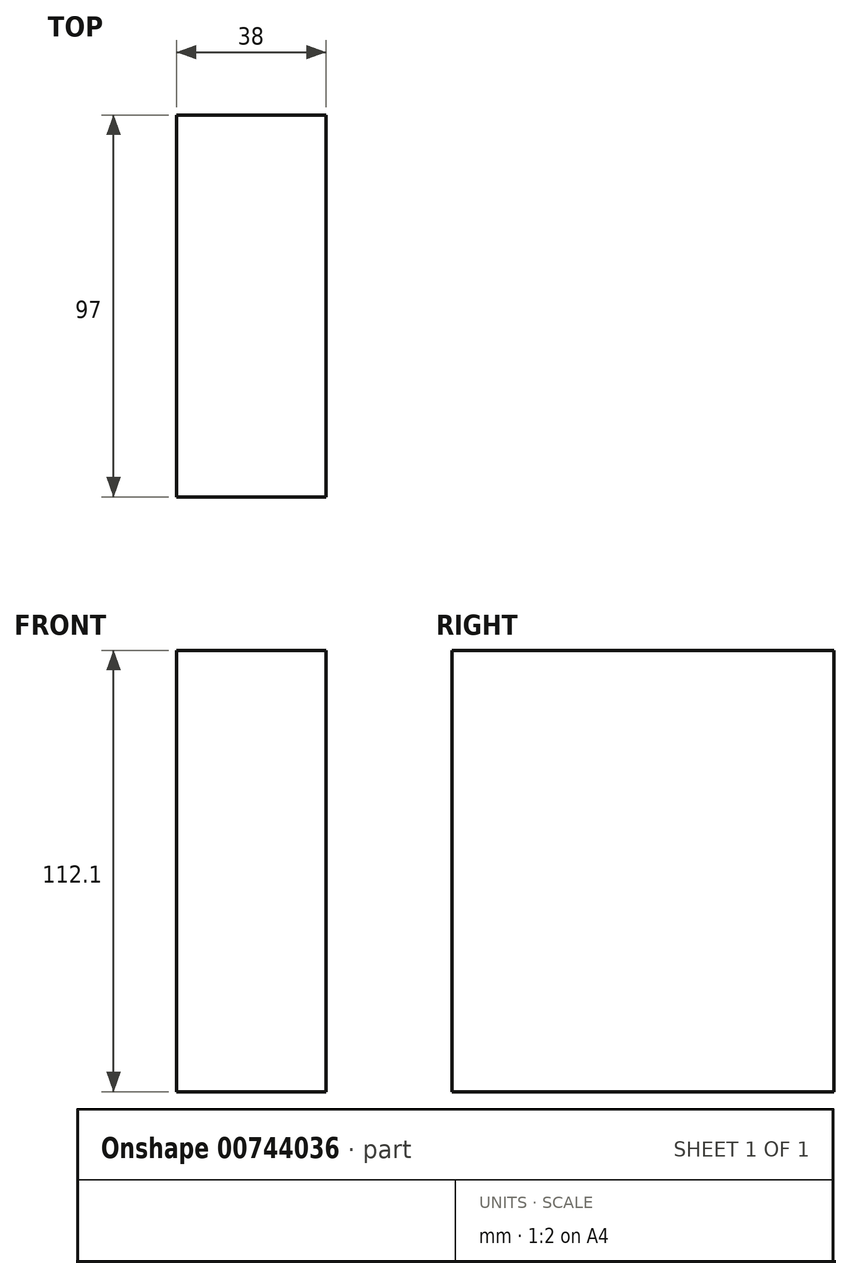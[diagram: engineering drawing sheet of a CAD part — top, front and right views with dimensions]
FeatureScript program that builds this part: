
annotation { "Feature Type Name" : "Feature", "Feature Type Description" : "" }
export const myFeature = defineFeature(function(context is Context, id is Id, definition is map)
    precondition{}
    {
        {
            var Q0;
            Q0=qCreatedBy(makeId("Top.planeOp"),FACE);
            var sketch = newSketch(context, id + "F0", { "sketchPlane" : qUnion([Q0])});
            skLineSegment(sketch, "E0.bottom", {"start": v(-19, -48.5) * mm, "end": v(19, -48.5) * mm});
            skLineSegment(sketch, "E0.top", {"start": v(-19, 48.5) * mm, "end": v(19, 48.5) * mm});
            skLineSegment(sketch, "E0.left", {"start": v(-19, -48.5) * mm, "end": v(-19, 48.5) * mm});
            skLineSegment(sketch, "E0.right", {"start": v(19, -48.5) * mm, "end": v(19, 48.5) * mm});
            skPoint(sketch, "E0.middle", {"position": v(0, 0) * mm});
            skSolve(sketch);
        }
        {
            var Q0;
            Q0=makeQuery(id+"F0.imprint","IMPRINT",FACE,{"disambiguationData":[TD([[makeQuery(id+"F0.imprint","IMPRINT",EDGE,{"derivedFrom":sQuery(id+"F0.wireOp",EDGE,"E0.bottom")}),1.0]])]});
            extrude(context, id + "F1", {"entities" : qUnion([Q0]), "depth" : 112.1 * mm, "offsetDistance" : 25 * mm});
        }
    });
